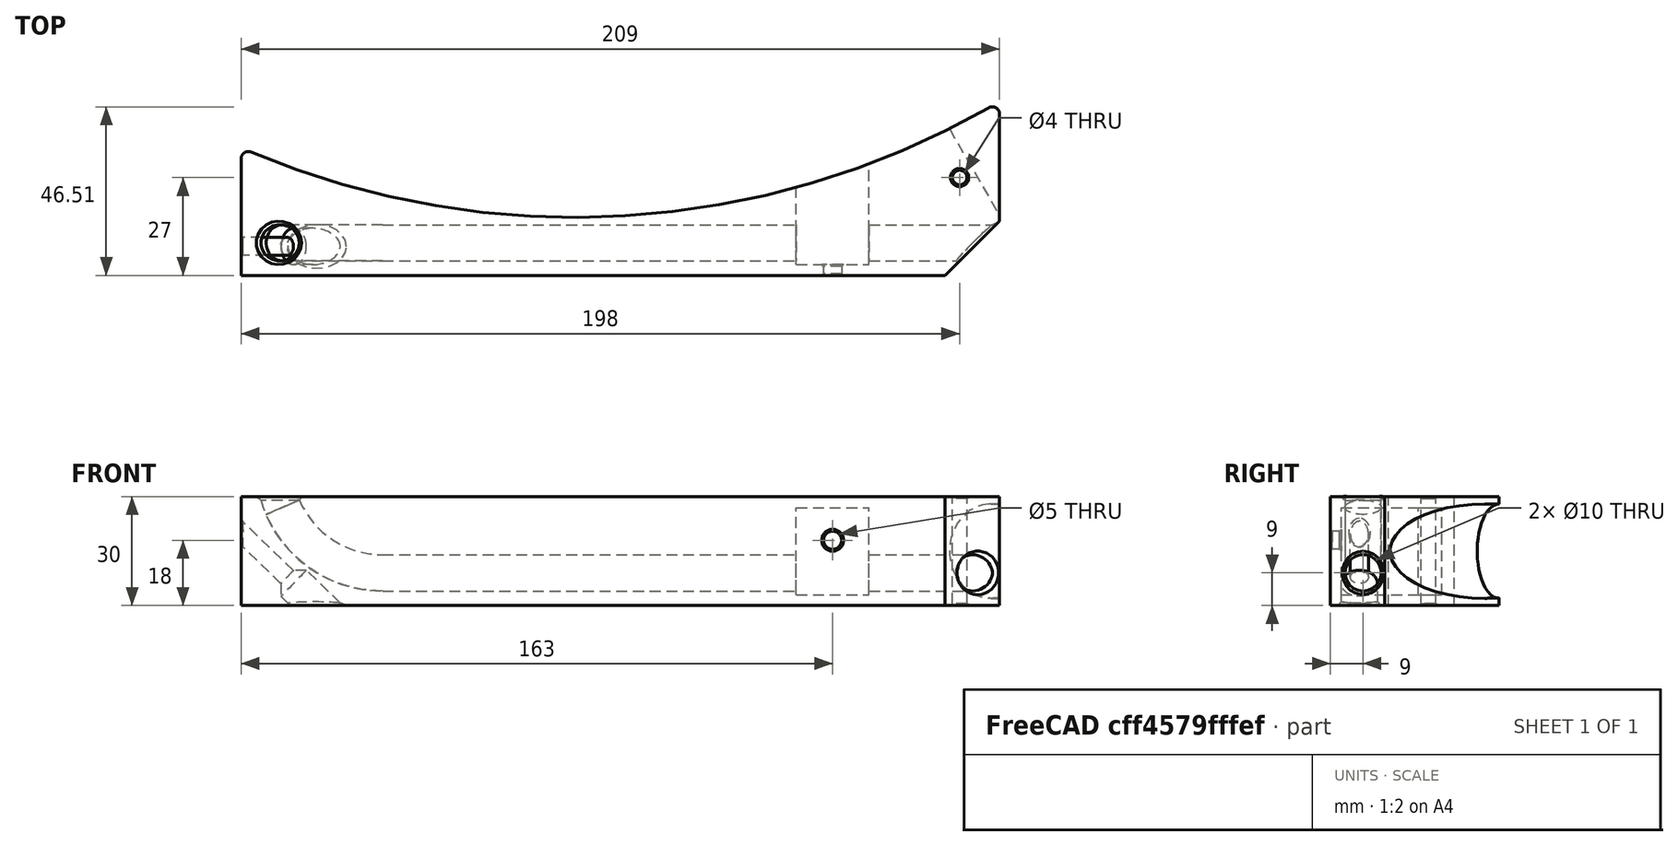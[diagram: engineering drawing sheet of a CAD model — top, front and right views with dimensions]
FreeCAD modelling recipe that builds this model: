
FCSTD DOCUMENT  (FreeCAD 0.19R24291 (Git))
Label: Support
License: Other
LicenseURL: https://www.gnu.org/licenses/gpl-3.0.en.html
objects: Part::Cylinder×7, Part::Chamfer×7, Part::Box×5, Part::MultiFuse×5, Part::Fuse×1, Part::Torus×1, Part::MultiCommon×1, Part::Cut×1, Part::Fillet×1
note: 29 computed .brp shape members not serialized (recipe doc carries the construction recipe); baked Part::Feature solids carry a one-line shape summary decoded from their .brp

FEATURE [Part::Cylinder] Cylinder
  Angle = 360
  AttacherType = Attacher::AttachEngine3D
  Height = 100
  Placement = pos=(0,230,-50) rot=(0,0,1;0rad)
  Radius = 230
FEATURE [Part::Box] Box  label="Cubexxx"
  AttacherType = Attacher::AttachEngine3D
  Height = 100
  Length = 10
  Placement = pos=(1000,-30,-50) rot=(0,0,1;0rad)
  Width = 40
FEATURE [Part::Cylinder] Cylinder001
  Angle = 360
  AttacherType = Attacher::AttachEngine3D
  Height = 56
  Placement = pos=(0,6,0) rot=(1,0,0;1.5708rad)
  Radius = 13
FEATURE [Part::MultiFuse] Fusion
  Placement = pos=(181.981,89.3488,0) rot=(0,0,1;0.912807rad)
  Shapes = -> [Cylinder,Cylinder001]
FEATURE [Part::Box] Box001  label="Cube001"
  AttacherType = Attacher::AttachEngine3D
  Height = 100
  Length = 49
  Placement = pos=(-141,-28,-50) rot=(0,0,1;0rad)
  Width = 54
FEATURE [Part::MultiFuse] Fusion001
  Placement = pos=(-87.6462,17.3544,0) rot=(0,0,-1;0.390954rad)
  Shapes = -> [Fusion,Box]
FEATURE [Part::Fuse] Fusion002
  Base = -> Box001
  Tool = -> Fusion001
FEATURE [Part::Box] Box002  label="Cube002"
  AttacherType = Attacher::AttachEngine3D
  Height = 30
  Length = 209
  Placement = pos=(-92,-16,-15) rot=(0,0,1;0rad)
  Width = 50
FEATURE [Part::Cylinder] Cylinder002
  Angle = 360
  AttacherType = Attacher::AttachEngine3D
  Height = 100
  Placement = pos=(106,11,-34) rot=(0,0,1;0rad)
  Radius = 2
FEATURE [Part::Cylinder] Cylinder003
  Angle = 360
  AttacherType = Attacher::AttachEngine3D
  Height = 300
  Placement = pos=(-53,-7,0) rot=(0,1,0;1.5708rad)
  Radius = 5
FEATURE [Part::Torus] Torus
  Angle1 = -180
  Angle2 = 180
  Angle3 = 360
  AttacherType = Attacher::AttachEngine3D
  Placement = pos=(-53,-7,30) rot=(1,0,0;1.5708rad)
  Radius1 = 30
  Radius2 = 5
FEATURE [Part::Box] Box003  label="Cube003"
  AttacherType = Attacher::AttachEngine3D
  Height = 42
  Length = 39
  Placement = pos=(-92,-16,-15) rot=(0,0,1;0rad)
  Width = 50
FEATURE [Part::Cylinder] Cylinder004
  Angle = 360
  AttacherType = Attacher::AttachEngine3D
  Height = 100
  Placement = pos=(-66,-8,-20) rot=(0,-1,0;0.802851rad)
  Radius = 2.5
FEATURE [Part::Cylinder] Cylinder005
  Angle = 360
  AttacherType = Attacher::AttachEngine3D
  Height = 20
  Placement = pos=(-52,-8,-20) rot=(0,-1,0;0.802851rad)
  Radius = 5
FEATURE [Part::Chamfer] Chamfer
  Base = -> Box002
  Edges = 1 edges r=15: [Edge5]
FEATURE [Part::Chamfer] Chamfer001
  Base = -> Cylinder005
  Edges = 1 edges r=4: [Edge1]
  Placement = pos=(-14,0,0) rot=(0,0,1;0rad)
FEATURE [Part::Box] Box004  label="Cube004"
  AttacherType = Attacher::AttachEngine3D
  Height = 24
  Length = 20
  Placement = pos=(0,-13,-12) rot=(0,0,1;0rad)
  Width = 52
FEATURE [Part::Cylinder] Cylinder006
  Angle = 360
  AttacherType = Attacher::AttachEngine3D
  Height = 35
  Placement = pos=(10,0,3) rot=(1,0,0;1.5708rad)
  Radius = 2.5
FEATURE [Part::MultiFuse] Fusion005
  Placement = pos=(61,0,0) rot=(0,0,1;0rad)
  Shapes = -> [Box004,Cylinder006]
FEATURE [Part::MultiCommon] Common
  Shapes = -> [Box003,Torus]
FEATURE [Part::MultiFuse] Fusion006
  Placement = pos=(0,0,-6) rot=(0,0,1;0rad)
  Shapes = -> [Common,Cylinder003]
FEATURE [Part::MultiFuse] Fusion007  label="holes"
  Shapes = -> [Fusion006,Fusion005,Chamfer001,Cylinder004,Cylinder002,Fusion002]
FEATURE [Part::Cut] Cut
  Base = -> Chamfer
  Tool = -> Fusion007
FEATURE [Part::Fillet] Fillet
  Base = -> Cut
  Edges = 3 edges r=2: [Edge2,Edge4,Edge15]
FEATURE [Part::Chamfer] Chamfer002
  Base = -> Fillet
  Edges = 2 edges r=0.5: [Edge34,Edge49]
FEATURE [Part::Chamfer] Chamfer003
  Base = -> Chamfer002
  Edges = 2 edges r=1: [Edge24,Edge27]
FEATURE [Part::Chamfer] Chamfer004
  Base = -> Chamfer003
  Edges = 2 edges r=0.5: [Edge9,Edge38]
FEATURE [Part::Chamfer] Chamfer005
  Base = -> Chamfer004
  Edges = 1 edges r=1: [Edge46]
FEATURE [Part::Chamfer] Chamfer006
  Base = -> Chamfer005
  Edges = 1 edges r=0.5: [Edge17]
